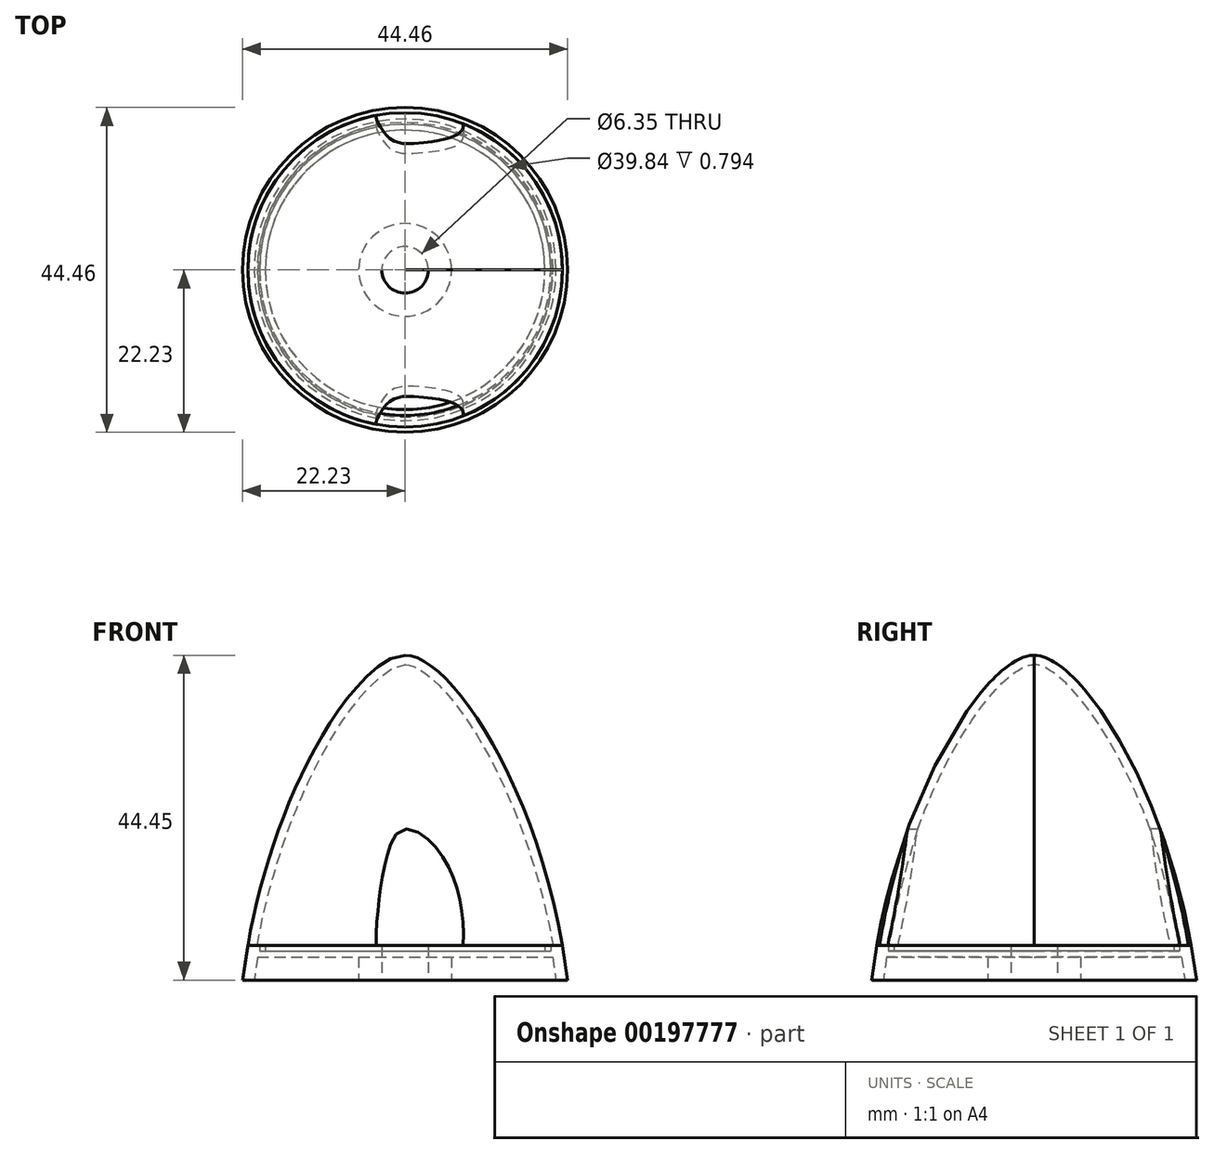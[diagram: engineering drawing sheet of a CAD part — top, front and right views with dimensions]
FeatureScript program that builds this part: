
annotation { "Feature Type Name" : "Feature", "Feature Type Description" : "" }
export const myFeature = defineFeature(function(context is Context, id is Id, definition is map)
    precondition{}
    {
        {
            var Q0;
            Q0=qCreatedBy(makeId("Front.planeOp"),FACE);
            var sketch = newSketch(context, id + "F0", { "sketchPlane" : qUnion([Q0])});
            skLineSegment(sketch, "E0", {"start": v(0, 0) * mm, "end": v(0, 44.45) * mm});
            skLineSegment(sketch, "E1", {"start": v(0, 0) * mm, "end": v(22.23, 0) * mm});
            skFitSpline(sketch, "E2", {"points": [v(0, 44.45) * mm, v(22.23, 0) * mm], "startDerivative": vector(19.05, 0) * mm, "endDerivative": vector(9.53, -76.2) * mm});
            skLineSegment(sketch, "E3", {"start": v(0, 4.76) * mm, "end": v(21.5, 4.76) * mm});
            skSolve(sketch);
        }
        {
            var Q0;
            Q0=qCreatedBy(makeId("Front.planeOp"),FACE);
            var sketch = newSketch(context, id + "F1", { "sketchPlane" : qUnion([Q0])});
            skLineSegment(sketch, "E4", {"start": v(3.17, 0) * mm, "end": v(3.17, 4.76) * mm});
            skLineSegment(sketch, "E5", {"start": v(3.18, 4.76) * mm, "end": v(19.13, 4.76) * mm});
            skLineSegment(sketch, "E6", {"start": v(19.13, 4.76) * mm, "end": v(19.13, 3.97) * mm});
            skLineSegment(sketch, "E7", {"start": v(19.13, 3.97) * mm, "end": v(19.92, 3.97) * mm});
            skLineSegment(sketch, "E8", {"start": v(19.92, 3.97) * mm, "end": v(19.92, 4.76) * mm});
            skLineSegment(sketch, "E9", {"start": v(19.92, 4.76) * mm, "end": v(21.5, 4.76) * mm});
            skLineSegment(sketch, "E10", {"start": v(21.5, 4.76) * mm, "end": v(22.22, 0) * mm});
            skLineSegment(sketch, "E11", {"start": v(22.23, 0) * mm, "end": v(20.64, 0) * mm});
            skLineSegment(sketch, "E12", {"start": v(6.35, 0) * mm, "end": v(3.18, 0) * mm});
            skLineSegment(sketch, "E13", {"start": v(6.35, 0) * mm, "end": v(6.35, 3.18) * mm});
            skLineSegment(sketch, "E14", {"start": v(6.35, 3.18) * mm, "end": v(20.16, 3.18) * mm});
            skLineSegment(sketch, "E15", {"start": v(20.16, 3.18) * mm, "end": v(20.64, 0) * mm});
            skSolve(sketch);
        }
        {
            var Q0;
            Q0=qCreatedBy(makeId("Front.planeOp"),FACE);
            var sketch = newSketch(context, id + "F2", { "sketchPlane" : qUnion([Q0])});
            skLineSegment(sketch, "E16", {"start": v(0, 4.76) * mm, "end": v(7.94, 4.76) * mm});
            skLineSegment(sketch, "E17", {"start": v(0, 0) * mm, "end": v(0, 20.64) * mm, "construction": true});
            skPoint(sketch, "E17.endSnap0", {"position": v(0, 4.76) * mm});
            skPoint(sketch, "E18.orphan", {"position": v(-7.94, 4.76) * mm});
            skLineSegment(sketch, "E19.MirrorCS", {"start": v(0, 4.76) * mm, "end": v(-7.94, 4.76) * mm});
            skFitSpline(sketch, "E20", {"points": [v(7.94, 4.76) * mm, v(4.76, 17.46) * mm, v(0, 20.64) * mm, v(-2.35, 17.46) * mm, v(-3.97, 4.76) * mm], "startDerivative": vector(2.48, 46.33) * mm, "endDerivative": vector(0.14, -33.74) * mm});
            skSolve(sketch);
        }
        {
            var Q0;
            {var subQ3=sQuery(id+"F0.wireOp",EDGE,"E3");Q0=makeQuery(id+"F0.imprint","IMPRINT",FACE,{"disambiguationData":[TD([[makeQuery(id+"F0.imprint","IMPRINT",EDGE,{"derivedFrom":subQ3}),1.0]])]});}
            var Q1;
            Q1=sQuery(id+"F0.wireOp",EDGE,"E0");
            revolve(context, id + "F3", {"surfaceOperationType" : NewSurfaceOperationType.NEW, "entities" : qUnion([Q0]), "axis" : qUnion([Q1]), "revolveType" : RevolveType.FULL});
        }
        {
            var Q0;
            Q0=makeQuery(id+"F3.opRevolve","SWEPT_FACE",FACE,{"disambiguationData":[OSD([sQuery(id+"F0.wireOp",EDGE,"E3")])]});
            shell(context, id + "F4", {"entities" : qUnion([Q0]), "thickness" : 1.27 * mm});
        }
        {
            var Q0;
            Q0=makeQuery(id+"F1.imprint","IMPRINT",FACE,{"disambiguationData":[TD([[makeQuery(id+"F1.imprint","IMPRINT",EDGE,{"derivedFrom":sQuery(id+"F1.wireOp",EDGE,"E4")}),-1.0]])]});
            var Q1;
            Q1=sQuery(id+"F0.wireOp",EDGE,"E0");
            revolve(context, id + "F5", {"entities" : qUnion([Q0]), "axis" : qUnion([Q1]), "revolveType" : RevolveType.FULL});
        }
        {
            var Q0;
            Q0 = qSketchRegion(id + "F2", true);
            var Q1;
            Q1=makeQuery(id+"F3.opRevolve","SWEPT_BODY",BODY,{"disambiguationData":[OSD([sQuery(id+"F0.wireOp",EDGE,"E0"),sQuery(id+"F0.wireOp",EDGE,"E2"),sQuery(id+"F0.wireOp",EDGE,"E3")])]});
            extrude(context, id + "F6", {"entities" : qUnion([Q0]), "operationType" : NewBodyOperationType.REMOVE, "endBound" : BoundingType.THROUGH_ALL, "endBoundEntityBody" : qUnion([Q1]), "depth" : 25.4 * mm, "offsetDistance" : 25.4 * mm});
        }
        {
            var Q0;
            Q0=makeQuery(id+"F2.imprint","IMPRINT",FACE,{"disambiguationData":[TD([[makeQuery(id+"F2.imprint","IMPRINT",EDGE,{"derivedFrom":sQuery(id+"F2.wireOp",EDGE,"E16")}),1.0]])]});
            var Q1;
            Q1=makeQuery(id+"F3.opRevolve","SWEPT_BODY",BODY,{"disambiguationData":[OSD([sQuery(id+"F0.wireOp",EDGE,"E0"),sQuery(id+"F0.wireOp",EDGE,"E2"),sQuery(id+"F0.wireOp",EDGE,"E3")])]});
            extrude(context, id + "F7", {"entities" : qUnion([Q0]), "operationType" : NewBodyOperationType.REMOVE, "endBound" : BoundingType.THROUGH_ALL, "oppositeDirection" : true, "endBoundEntityBody" : qUnion([Q1]), "depth" : 25.4 * mm});
        }
    });
